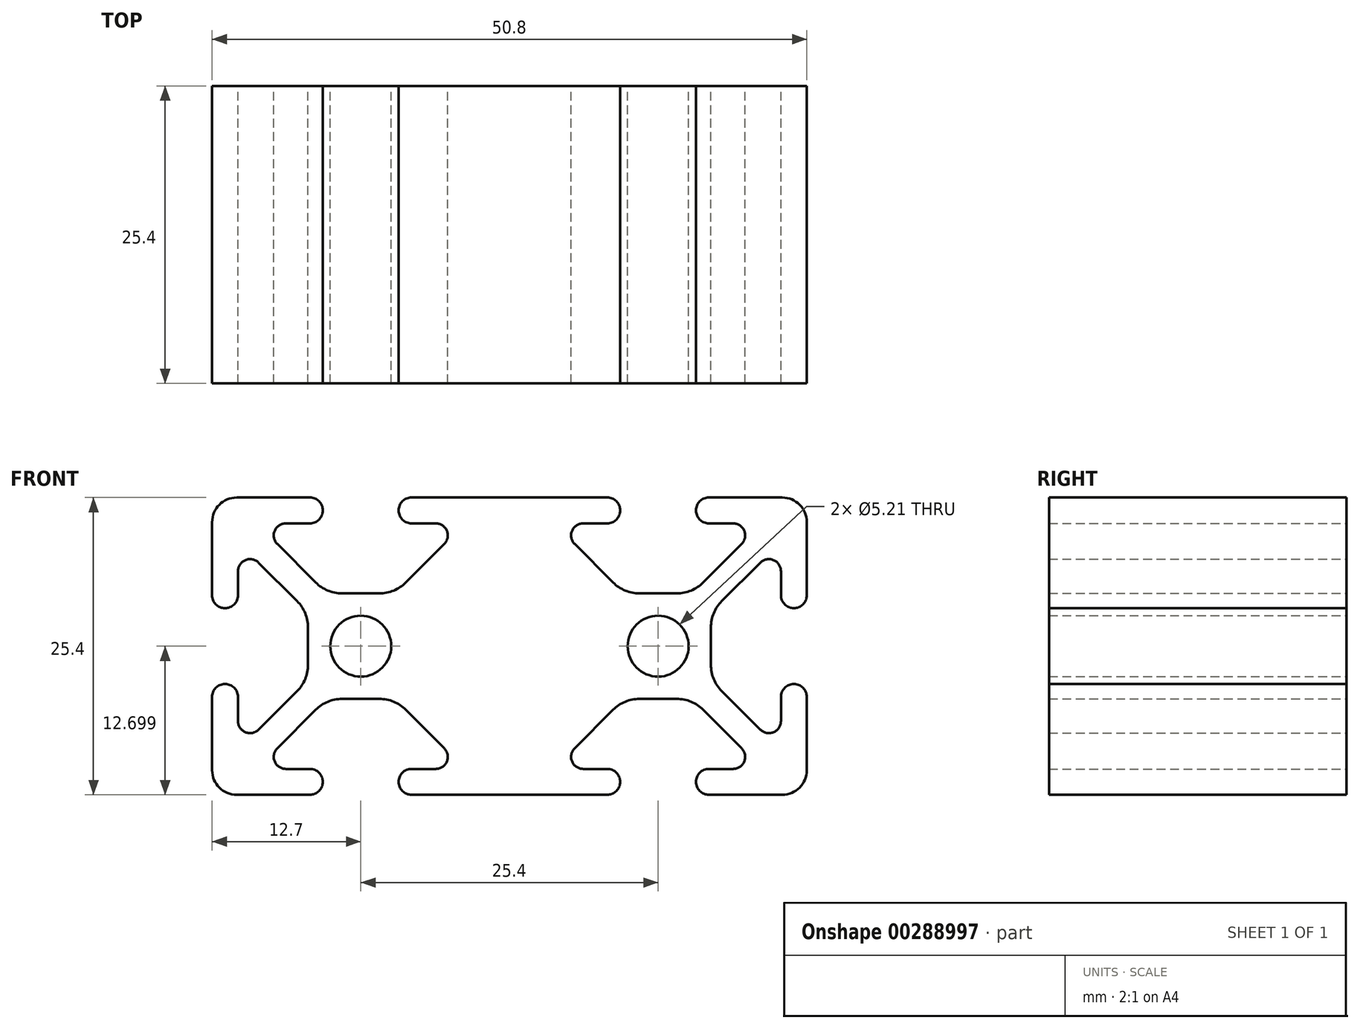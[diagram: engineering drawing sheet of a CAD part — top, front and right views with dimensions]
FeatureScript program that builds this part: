
annotation { "Feature Type Name" : "Feature", "Feature Type Description" : "" }
export const myFeature = defineFeature(function(context is Context, id is Id, definition is map)
    precondition{}
    {
        {
            var Q0;
            Q0=qCreatedBy(makeId("Front.planeOp"),FACE);
            var sketch = newSketch(context, id + "F0", { "sketchPlane" : qUnion([Q0])});
            skArc(sketch, "E0", {"start": v(-23.3, 12.83) * mm, "mid": v(-24.78, 12.21) * mm, "end": v(-25.4, 10.72) * mm});
            skArc(sketch, "E1", {"start": v(-25.4, 4.47) * mm, "mid": v(-24.3, 3.37) * mm, "end": v(-23.2, 4.47) * mm});
            skArc(sketch, "E2", {"start": v(-17.04, 10.62) * mm, "mid": v(-15.94, 11.72) * mm, "end": v(-17.04, 12.83) * mm});
            skArc(sketch, "E3", {"start": v(-21.43, 7.26) * mm, "mid": v(-22.55, 7.48) * mm, "end": v(-23.2, 6.53) * mm});
            skArc(sketch, "E4", {"start": v(-19.1, 10.62) * mm, "mid": v(-20.05, 9.98) * mm, "end": v(-19.83, 8.85) * mm});
            skLineSegment(sketch, "E5", {"start": v(-25.4, 10.72) * mm, "end": v(-25.4, 4.47) * mm});
            skLineSegment(sketch, "E6", {"start": v(-23.3, 12.83) * mm, "end": v(-17.04, 12.83) * mm});
            skLineSegment(sketch, "E7", {"start": v(-23.2, 4.47) * mm, "end": v(-23.2, 6.53) * mm});
            skLineSegment(sketch, "E8", {"start": v(-17.04, 10.62) * mm, "end": v(-19.1, 10.62) * mm});
            skLineSegment(sketch, "E9", {"start": v(-9.14, 7.56) * mm, "end": v(-7.92, 7.56) * mm, "construction": true});
            skLineSegment(sketch, "E10", {"start": v(-11.26, 3.37) * mm, "end": v(-9.98, 3.37) * mm, "construction": true});
            skLineSegment(sketch, "E11", {"start": v(-20.13, 8.37) * mm, "end": v(-20.13, 6.25) * mm, "construction": true});
            skLineSegment(sketch, "E12", {"start": v(-15.94, 9.7) * mm, "end": v(-15.94, 7.59) * mm, "construction": true});
            skLineSegment(sketch, "E13.bottom", {"start": v(-11.1, 4.64) * mm, "end": v(-14.3, 4.64) * mm});
            skLineSegment(sketch, "E13.top", {"start": v(-11.1, -4.38) * mm, "end": v(-14.3, -4.38) * mm});
            skLineSegment(sketch, "E13.left", {"start": v(-8.2, 1.73) * mm, "end": v(-8.2, -1.47) * mm});
            skLineSegment(sketch, "E13.right", {"start": v(-17.2, 1.73) * mm, "end": v(-17.2, -1.47) * mm});
            skPoint(sketch, "E13.middle", {"position": v(-12.7, 0.13) * mm});
            skLineSegment(sketch, "E14", {"start": v(-21.43, 7.26) * mm, "end": v(-18.14, 3.97) * mm});
            skLineSegment(sketch, "E15", {"start": v(-19.83, 8.85) * mm, "end": v(-16.54, 5.57) * mm});
            skArc(sketch, "E16.filletArc", {"start": v(-16.54, 5.57) * mm, "mid": v(-15.51, 4.88) * mm, "end": v(-14.3, 4.64) * mm});
            skArc(sketch, "E17.filletArc", {"start": v(-17.2, 1.73) * mm, "mid": v(-17.45, 2.94) * mm, "end": v(-18.14, 3.97) * mm});
            skLineSegment(sketch, "E18", {"start": v(-7.21, 0.13) * mm, "end": v(-22.59, 0.13) * mm, "construction": true});
            skPoint(sketch, "E18.startSnap0", {"position": v(-12.6, 0.13) * mm});
            skPoint(sketch, "E19", {"position": v(-12.7, -4.38) * mm});
            skLineSegment(sketch, "E20", {"start": v(-12.7, -6.63) * mm, "end": v(-12.7, 5.96) * mm, "construction": true});
            skLineSegment(sketch, "E21.MirrorCS", {"start": v(-16.26, 7.56) * mm, "end": v(-17.48, 7.56) * mm, "construction": true});
            skLineSegment(sketch, "E22.MirrorCS", {"start": v(-5.27, 8.37) * mm, "end": v(-5.27, 6.25) * mm, "construction": true});
            skArc(sketch, "E23.MirrorCS", {"start": v(-8.86, 5.57) * mm, "mid": v(-9.89, 4.88) * mm, "end": v(-11.1, 4.64) * mm});
            skLineSegment(sketch, "E24.MirrorCS", {"start": v(-9.46, 9.7) * mm, "end": v(-9.46, 7.59) * mm, "construction": true});
            skLineSegment(sketch, "E25.MirrorCS", {"start": v(-14.14, 3.37) * mm, "end": v(-15.42, 3.37) * mm, "construction": true});
            skArc(sketch, "E26.MirrorCS", {"start": v(-8.36, 10.62) * mm, "mid": v(-9.46, 11.72) * mm, "end": v(-8.36, 12.83) * mm});
            skLineSegment(sketch, "E27.MirrorCS", {"start": v(2.1, 12.83) * mm, "end": v(-8.36, 12.83) * mm});
            skArc(sketch, "E28.MirrorCS", {"start": v(-6.3, 10.62) * mm, "mid": v(-5.35, 9.98) * mm, "end": v(-5.57, 8.85) * mm});
            skLineSegment(sketch, "E29.MirrorCS", {"start": v(-5.57, 8.85) * mm, "end": v(-8.86, 5.57) * mm});
            skLineSegment(sketch, "E30.MirrorCS", {"start": v(-8.36, 10.62) * mm, "end": v(-6.3, 10.62) * mm});
            skLineSegment(sketch, "E31.MirrorCS", {"start": v(-9.14, -7.3) * mm, "end": v(-7.92, -7.3) * mm, "construction": true});
            skArc(sketch, "E32.MirrorCS", {"start": v(-16.54, -5.3) * mm, "mid": v(-15.51, -4.62) * mm, "end": v(-14.3, -4.38) * mm});
            skArc(sketch, "E33.MirrorCS", {"start": v(-23.3, -12.57) * mm, "mid": v(-24.78, -11.95) * mm, "end": v(-25.4, -10.46) * mm});
            skArc(sketch, "E34.MirrorCS", {"start": v(-21.43, -7) * mm, "mid": v(-22.55, -7.23) * mm, "end": v(-23.2, -6.27) * mm});
            skArc(sketch, "E35.MirrorCS", {"start": v(-19.1, -10.36) * mm, "mid": v(-20.05, -9.72) * mm, "end": v(-19.83, -8.6) * mm});
            skLineSegment(sketch, "E36.MirrorCS", {"start": v(-15.94, -9.45) * mm, "end": v(-15.94, -7.33) * mm, "construction": true});
            skArc(sketch, "E37.MirrorCS", {"start": v(-17.2, -1.47) * mm, "mid": v(-17.45, -2.68) * mm, "end": v(-18.14, -3.71) * mm});
            skLineSegment(sketch, "E38.MirrorCS", {"start": v(-25.4, -10.46) * mm, "end": v(-25.4, -4.21) * mm});
            skLineSegment(sketch, "E39.MirrorCS", {"start": v(-11.26, -3.1) * mm, "end": v(-9.98, -3.1) * mm, "construction": true});
            skLineSegment(sketch, "E40.MirrorCS", {"start": v(-20.13, -8.11) * mm, "end": v(-20.13, -6) * mm, "construction": true});
            skLineSegment(sketch, "E41.MirrorCS", {"start": v(-17.04, -10.36) * mm, "end": v(-19.1, -10.36) * mm});
            skLineSegment(sketch, "E42.MirrorCS", {"start": v(-23.3, -12.57) * mm, "end": v(-17.04, -12.57) * mm});
            skLineSegment(sketch, "E43.MirrorCS", {"start": v(-23.2, -4.21) * mm, "end": v(-23.2, -6.27) * mm});
            skArc(sketch, "E44.MirrorCS", {"start": v(-25.4, -4.21) * mm, "mid": v(-24.3, -3.1) * mm, "end": v(-23.2, -4.21) * mm});
            skLineSegment(sketch, "E45.MirrorCS", {"start": v(-21.43, -7) * mm, "end": v(-18.14, -3.71) * mm});
            skLineSegment(sketch, "E46.MirrorCS", {"start": v(-19.83, -8.6) * mm, "end": v(-16.54, -5.3) * mm});
            skArc(sketch, "E47.MirrorCS", {"start": v(-17.04, -10.36) * mm, "mid": v(-15.94, -11.47) * mm, "end": v(-17.04, -12.57) * mm});
            skLineSegment(sketch, "E48.MirrorCS", {"start": v(-16.26, -7.3) * mm, "end": v(-17.48, -7.3) * mm, "construction": true});
            skArc(sketch, "E49.MirrorCS", {"start": v(-8.36, -10.36) * mm, "mid": v(-9.46, -11.47) * mm, "end": v(-8.36, -12.57) * mm});
            skLineSegment(sketch, "E50.MirrorCS", {"start": v(-14.14, -3.1) * mm, "end": v(-15.42, -3.1) * mm, "construction": true});
            skLineSegment(sketch, "E51.MirrorCS", {"start": v(-5.57, -8.6) * mm, "end": v(-8.86, -5.3) * mm});
            skLineSegment(sketch, "E52.MirrorCS", {"start": v(-5.27, -8.11) * mm, "end": v(-5.27, -6) * mm, "construction": true});
            skLineSegment(sketch, "E53.MirrorCS", {"start": v(-9.46, -9.45) * mm, "end": v(-9.46, -7.33) * mm, "construction": true});
            skLineSegment(sketch, "E54.MirrorCS", {"start": v(-8.36, -10.36) * mm, "end": v(-6.3, -10.36) * mm});
            skArc(sketch, "E55.MirrorCS", {"start": v(-8.86, -5.3) * mm, "mid": v(-9.89, -4.62) * mm, "end": v(-11.1, -4.38) * mm});
            skLineSegment(sketch, "E56.MirrorCS", {"start": v(2.1, -12.57) * mm, "end": v(-8.36, -12.57) * mm});
            skLineSegment(sketch, "E57.MirrorCS", {"start": v(0, -10.46) * mm, "end": v(0, -4.21) * mm, "construction": true});
            skArc(sketch, "E58.MirrorCS", {"start": v(-6.3, -10.36) * mm, "mid": v(-5.35, -9.72) * mm, "end": v(-5.57, -8.6) * mm});
            skCircle(sketch, "E59", {"center": v(-12.7, 0.13) * mm, "radius": 2.6 * mm});
            skPoint(sketch, "E60.MirrorP", {"position": v(12.7, 0.13) * mm});
            skLineSegment(sketch, "E61.MirrorCS", {"start": v(17.04, 10.62) * mm, "end": v(19.1, 10.62) * mm});
            skLineSegment(sketch, "E62.MirrorCS", {"start": v(17.04, -10.36) * mm, "end": v(19.1, -10.36) * mm});
            skLineSegment(sketch, "E63.MirrorCS", {"start": v(11.1, 4.64) * mm, "end": v(14.3, 4.64) * mm});
            skArc(sketch, "E64.MirrorCS", {"start": v(25.4, 4.47) * mm, "mid": v(24.3, 3.37) * mm, "end": v(23.2, 4.47) * mm});
            skArc(sketch, "E65.MirrorCS", {"start": v(17.04, 10.62) * mm, "mid": v(15.94, 11.72) * mm, "end": v(17.04, 12.83) * mm});
            skArc(sketch, "E66.MirrorCS", {"start": v(6.3, -10.36) * mm, "mid": v(5.35, -9.72) * mm, "end": v(5.57, -8.6) * mm});
            skLineSegment(sketch, "E67.MirrorCS", {"start": v(16.26, -7.3) * mm, "end": v(17.48, -7.3) * mm, "construction": true});
            skArc(sketch, "E68.MirrorCS", {"start": v(21.43, 7.26) * mm, "mid": v(22.55, 7.48) * mm, "end": v(23.2, 6.53) * mm});
            skArc(sketch, "E69.MirrorCS", {"start": v(16.54, -5.3) * mm, "mid": v(15.51, -4.62) * mm, "end": v(14.3, -4.38) * mm});
            skLineSegment(sketch, "E70.MirrorCS", {"start": v(5.27, 8.37) * mm, "end": v(5.27, 6.25) * mm, "construction": true});
            skLineSegment(sketch, "E71.MirrorCS", {"start": v(23.3, -12.57) * mm, "end": v(17.04, -12.57) * mm});
            skLineSegment(sketch, "E72.MirrorCS", {"start": v(20.13, 8.37) * mm, "end": v(20.13, 6.25) * mm, "construction": true});
            skLineSegment(sketch, "E73.MirrorCS", {"start": v(15.94, 9.7) * mm, "end": v(15.94, 7.59) * mm, "construction": true});
            skArc(sketch, "E74.MirrorCS", {"start": v(8.36, -10.36) * mm, "mid": v(9.46, -11.47) * mm, "end": v(8.36, -12.57) * mm});
            skArc(sketch, "E75.MirrorCS", {"start": v(23.3, -12.57) * mm, "mid": v(24.78, -11.95) * mm, "end": v(25.4, -10.46) * mm});
            skLineSegment(sketch, "E76.MirrorCS", {"start": v(14.14, -3.1) * mm, "end": v(15.42, -3.1) * mm, "construction": true});
            skArc(sketch, "E77.MirrorCS", {"start": v(21.43, -7) * mm, "mid": v(22.55, -7.23) * mm, "end": v(23.2, -6.27) * mm});
            skArc(sketch, "E78.MirrorCS", {"start": v(8.86, 5.57) * mm, "mid": v(9.89, 4.88) * mm, "end": v(11.1, 4.64) * mm});
            skLineSegment(sketch, "E79.MirrorCS", {"start": v(9.46, 9.7) * mm, "end": v(9.46, 7.59) * mm, "construction": true});
            skLineSegment(sketch, "E80.MirrorCS", {"start": v(23.2, -4.21) * mm, "end": v(23.2, -6.27) * mm});
            skLineSegment(sketch, "E81.MirrorCS", {"start": v(15.94, -9.45) * mm, "end": v(15.94, -7.33) * mm, "construction": true});
            skArc(sketch, "E82.MirrorCS", {"start": v(19.1, -10.36) * mm, "mid": v(20.05, -9.72) * mm, "end": v(19.83, -8.6) * mm});
            skLineSegment(sketch, "E83.MirrorCS", {"start": v(5.57, 8.85) * mm, "end": v(8.86, 5.57) * mm});
            skLineSegment(sketch, "E84.MirrorCS", {"start": v(7.21, 0.13) * mm, "end": v(22.59, 0.13) * mm, "construction": true});
            skArc(sketch, "E85.MirrorCS", {"start": v(25.4, -4.21) * mm, "mid": v(24.3, -3.1) * mm, "end": v(23.2, -4.21) * mm});
            skLineSegment(sketch, "E86.MirrorCS", {"start": v(8.36, 10.62) * mm, "end": v(6.3, 10.62) * mm});
            skLineSegment(sketch, "E87.MirrorCS", {"start": v(12.7, -6.63) * mm, "end": v(12.7, 5.96) * mm, "construction": true});
            skLineSegment(sketch, "E88.MirrorCS", {"start": v(25.4, -10.46) * mm, "end": v(25.4, -4.21) * mm});
            skLineSegment(sketch, "E89.MirrorCS", {"start": v(9.14, -7.3) * mm, "end": v(7.92, -7.3) * mm, "construction": true});
            skArc(sketch, "E90.MirrorCS", {"start": v(8.86, -5.3) * mm, "mid": v(9.89, -4.62) * mm, "end": v(11.1, -4.38) * mm});
            skLineSegment(sketch, "E91.MirrorCS", {"start": v(16.26, 7.56) * mm, "end": v(17.48, 7.56) * mm, "construction": true});
            skLineSegment(sketch, "E92.MirrorCS", {"start": v(11.26, -3.1) * mm, "end": v(9.98, -3.1) * mm, "construction": true});
            skLineSegment(sketch, "E93.MirrorCS", {"start": v(8.36, -10.36) * mm, "end": v(6.3, -10.36) * mm});
            skLineSegment(sketch, "E94.MirrorCS", {"start": v(21.43, -7) * mm, "end": v(18.14, -3.71) * mm});
            skLineSegment(sketch, "E95.MirrorCS", {"start": v(9.46, -9.45) * mm, "end": v(9.46, -7.33) * mm, "construction": true});
            skLineSegment(sketch, "E96.MirrorCS", {"start": v(14.14, 3.37) * mm, "end": v(15.42, 3.37) * mm, "construction": true});
            skArc(sketch, "E97.MirrorCS", {"start": v(17.2, 1.73) * mm, "mid": v(17.45, 2.94) * mm, "end": v(18.14, 3.97) * mm});
            skCircle(sketch, "E98.MirrorC", {"center": v(12.7, 0.13) * mm, "radius": 2.6 * mm});
            skLineSegment(sketch, "E99.MirrorCS", {"start": v(2.1, -12.57) * mm, "end": v(8.36, -12.57) * mm});
            skLineSegment(sketch, "E100.MirrorCS", {"start": v(2.1, 12.83) * mm, "end": v(8.36, 12.83) * mm});
            skLineSegment(sketch, "E101.MirrorCS", {"start": v(20.13, -8.11) * mm, "end": v(20.13, -6) * mm, "construction": true});
            skLineSegment(sketch, "E102.MirrorCS", {"start": v(21.43, 7.26) * mm, "end": v(18.14, 3.97) * mm});
            skLineSegment(sketch, "E103.MirrorCS", {"start": v(19.83, -8.6) * mm, "end": v(16.54, -5.3) * mm});
            skLineSegment(sketch, "E104.MirrorCS", {"start": v(17.2, 1.73) * mm, "end": v(17.2, -1.47) * mm});
            skArc(sketch, "E105.MirrorCS", {"start": v(8.36, 10.62) * mm, "mid": v(9.46, 11.72) * mm, "end": v(8.36, 12.83) * mm});
            skPoint(sketch, "E106.MirrorP", {"position": v(12.6, 0.13) * mm});
            skLineSegment(sketch, "E107.MirrorCS", {"start": v(5.27, -8.11) * mm, "end": v(5.27, -6) * mm, "construction": true});
            skArc(sketch, "E108.MirrorCS", {"start": v(17.2, -1.47) * mm, "mid": v(17.45, -2.68) * mm, "end": v(18.14, -3.71) * mm});
            skLineSegment(sketch, "E109.MirrorCS", {"start": v(5.57, -8.6) * mm, "end": v(8.86, -5.3) * mm});
            skArc(sketch, "E110.MirrorCS", {"start": v(6.3, 10.62) * mm, "mid": v(5.35, 9.98) * mm, "end": v(5.57, 8.85) * mm});
            skPoint(sketch, "E111.MirrorP", {"position": v(12.7, -4.38) * mm});
            skArc(sketch, "E112.MirrorCS", {"start": v(16.54, 5.57) * mm, "mid": v(15.51, 4.88) * mm, "end": v(14.3, 4.64) * mm});
            skLineSegment(sketch, "E113.MirrorCS", {"start": v(11.26, 3.37) * mm, "end": v(9.98, 3.37) * mm, "construction": true});
            skLineSegment(sketch, "E114.MirrorCS", {"start": v(9.14, 7.56) * mm, "end": v(7.92, 7.56) * mm, "construction": true});
            skLineSegment(sketch, "E115.MirrorCS", {"start": v(23.2, 4.47) * mm, "end": v(23.2, 6.53) * mm});
            skLineSegment(sketch, "E116.MirrorCS", {"start": v(23.3, 12.83) * mm, "end": v(17.04, 12.83) * mm});
            skLineSegment(sketch, "E117.MirrorCS", {"start": v(25.4, 10.72) * mm, "end": v(25.4, 4.47) * mm});
            skArc(sketch, "E118.MirrorCS", {"start": v(19.1, 10.62) * mm, "mid": v(20.05, 9.98) * mm, "end": v(19.83, 8.85) * mm});
            skArc(sketch, "E119.MirrorCS", {"start": v(23.3, 12.83) * mm, "mid": v(24.78, 12.21) * mm, "end": v(25.4, 10.72) * mm});
            skLineSegment(sketch, "E120.MirrorCS", {"start": v(8.2, 1.73) * mm, "end": v(8.2, -1.47) * mm});
            skLineSegment(sketch, "E121.MirrorCS", {"start": v(11.1, -4.38) * mm, "end": v(14.3, -4.38) * mm});
            skLineSegment(sketch, "E122.MirrorCS", {"start": v(19.83, 8.85) * mm, "end": v(16.54, 5.57) * mm});
            skArc(sketch, "E123.MirrorCS", {"start": v(17.04, -10.36) * mm, "mid": v(15.94, -11.47) * mm, "end": v(17.04, -12.57) * mm});
            skPoint(sketch, "E124.orphan", {"position": v(-2.1, 12.83) * mm});
            skPoint(sketch, "E125.orphan", {"position": v(-2.1, -12.57) * mm});
            skPoint(sketch, "E126", {"position": v(25.4, 12.83) * mm});
            skPoint(sketch, "E127", {"position": v(25.4, -12.57) * mm});
            skPoint(sketch, "E128", {"position": v(-25.4, -12.57) * mm});
            skPoint(sketch, "E129", {"position": v(-25.4, 12.83) * mm});
            skSolve(sketch);
        }
        {
            var Q0;
            Q0=makeQuery(id+"F0.imprint","IMPRINT",FACE,{"disambiguationData":[TD([[makeQuery(id+"F0.imprint","IMPRINT",EDGE,{"derivedFrom":sQuery(id+"F0.wireOp",EDGE,"E0")}),1.0]])]});
            extrude(context, id + "F1", {"entities" : qUnion([Q0]), "depth" : 25.4 * mm});
        }
    });
